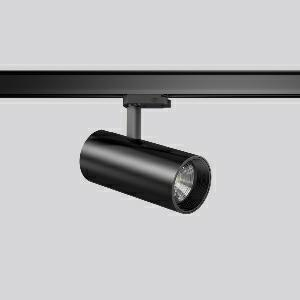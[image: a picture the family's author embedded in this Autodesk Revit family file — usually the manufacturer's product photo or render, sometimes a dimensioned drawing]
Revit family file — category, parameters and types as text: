
# Revit family: deecos_s_mini_742198_003_eba2
name_source: partatom
category: Lighting Fixtures
units: mm (PartAtom-declared; Revit-internal decimal feet)

## family parameters
Cut with Voids When Loaded = No
Host = Face
Light Source = No
Part Type = Normal
Room Calculation Point = No
Round Connector Dimension = Use Diameter
Shared = No

## types (1)
- DEECOS S mini (1 x LED Modul 930, 2250 lm, 3000)
    Apparent Load = 20 VA
    Approval mark = CE
    CIE Flux Codes = 99 100 100 100 100
    Color Rendering = 90
    Color Temperature = 3000
    Default Elevation = 1800 mm
    Description = Series: DEECOS S mini
LED surface-mounted projector in modern design with no visible cooling ribs. Housing: die-cast aluminium, powder-coated. Rotation range: 356°. Swivel range: 90°. Black plastic ring and recessed LED to prevent glare from the side. Optical assembly with lens made of plastic (polycarbonate) for the best homogeneous light distribution - can be changed without tools. Best colour rendering index Ra>90. With multi adaptor for 3-circuit tracks 230 V. Suitable for Track on ceiling, Wall track. High quality converter without flickering and stroboscopic effect. The following accessories can be mounted without use of tools: interchangeable lenses, decorative glasses, honeycomb louvre, clear and frosted diffusers, white interchangeable plastic ring. 
Colour: deep black, matt (RAL 9005)
Diameter: 87 mm
Height: 214 mm
Lamp: LED
Socket: without socket
Colour temperature: 3000K
Colour rendering index (CRI): 92
System power: 20 W
Rated luminous flux: 2250 lm
Luminous efficiency: 113 lm/W
Control gear: Regulated power supply
Protection class: I
Type of protection: IP 20
    Height = 214 mm
    Lamp = 1 x LED Modul 930
    Lamp Light Flux = 2250 lm
    Lamp count = 1
    Length = 87 mm
    Lifetime = 50000 h
    Luminous efficacy = 113 lm/W
    Manufacturer = RZB
    ModVariant = No
    Model = 742198.003
    Mounting Place = Ceiling
    Mounting Type = Rail mounted
    Number of Poles = 1
    OnlyDefault = Yes
    Power Factor = 1
    Product Name = DEECOS S mini
    Product group = Track mounted projectors
    ProductGroupID = 301
    Protection Class = Protection class I
    Protection Degree = IP 20
    RLX_Detail_Level = 1
    RLX_Emergency_Light_Flux = 0 lm
    RLX_Emergency_Type = 0
    RLX_Emergency_Type_DB = No
    RlxData = <blob elided: 38769 chars, md5=db1d7319>
    Socket = socket
    Standby Power = 0 W
    System Light Flux = 2250 lm
    System Power = 20 W
    Type Comments = Product without accessories
    Type Image = 741930.003.jpg
    URL = http://relux.com
    VarID = ---
    Voltage = 230 V
    Voltage Range = 220-240 V
    Weight = 0.00 kg
    Width = 0 mm  [stored 0 ft]

note: [stored X ft] marks values corroborated as IEEE doubles in the binary element streams (Revit-internal decimal feet)

## geometry (parser evidence)
native form markers: Blend x4, Sweep x12
no freeform markers — native parametric forms only
